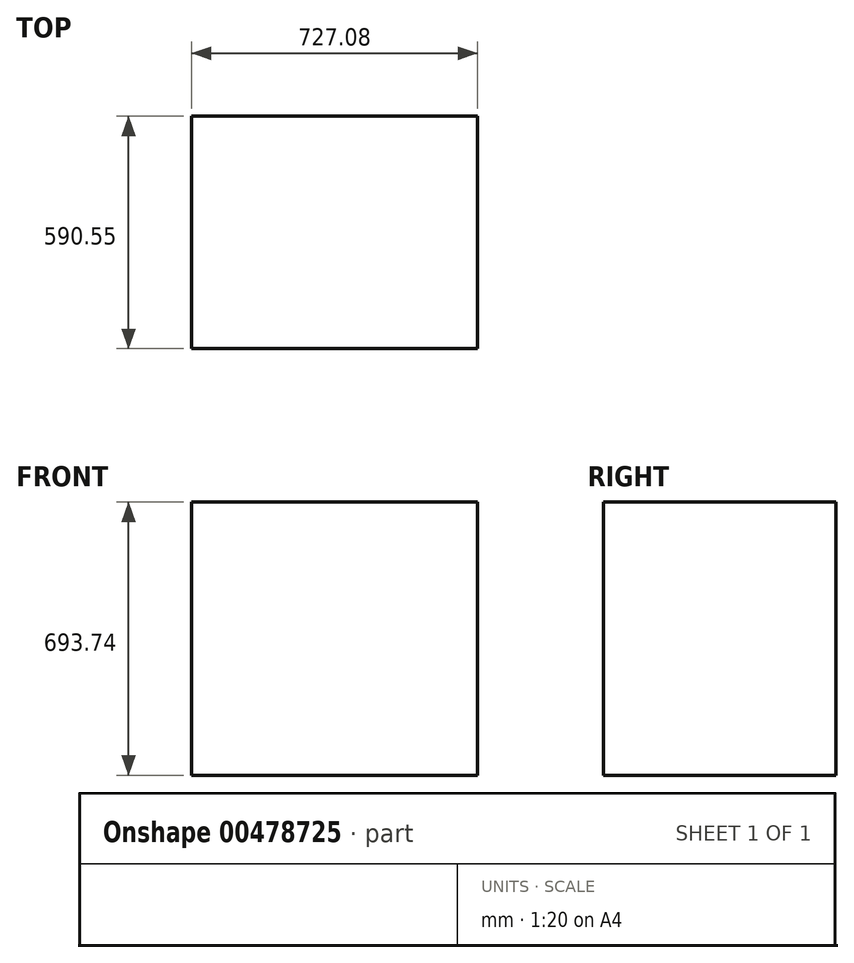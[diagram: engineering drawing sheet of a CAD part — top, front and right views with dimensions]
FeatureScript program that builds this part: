
annotation { "Feature Type Name" : "Feature", "Feature Type Description" : "" }
export const myFeature = defineFeature(function(context is Context, id is Id, definition is map)
    precondition{}
    {
        {
            var Q0;
            Q0=qCreatedBy(makeId("Front.planeOp"),FACE);
            var sketch = newSketch(context, id + "F0", { "sketchPlane" : qUnion([Q0])});
            skLineSegment(sketch, "E0.bottom", {"start": v(-363.54, -346.87) * mm, "end": v(363.54, -346.87) * mm});
            skLineSegment(sketch, "E0.top", {"start": v(-363.54, 346.87) * mm, "end": v(363.54, 346.87) * mm});
            skLineSegment(sketch, "E0.left", {"start": v(-363.54, -346.87) * mm, "end": v(-363.54, 346.87) * mm});
            skLineSegment(sketch, "E0.right", {"start": v(363.54, -346.87) * mm, "end": v(363.54, 346.87) * mm});
            skLineSegment(sketch, "E1", {"start": v(-363.54, 346.87) * mm, "end": v(363.54, -346.87) * mm, "construction": true});
            skPoint(sketch, "E2", {"position": v(0, 0) * mm});
            skSolve(sketch);
        }
        {
            var Q0;
            Q0 = qSketchRegion(id + "F0", true);
            extrude(context, id + "F1", {"entities" : qUnion([Q0]), "depth" : 590.55 * mm, "offsetDistance" : 25.4 * mm});
        }
    });
